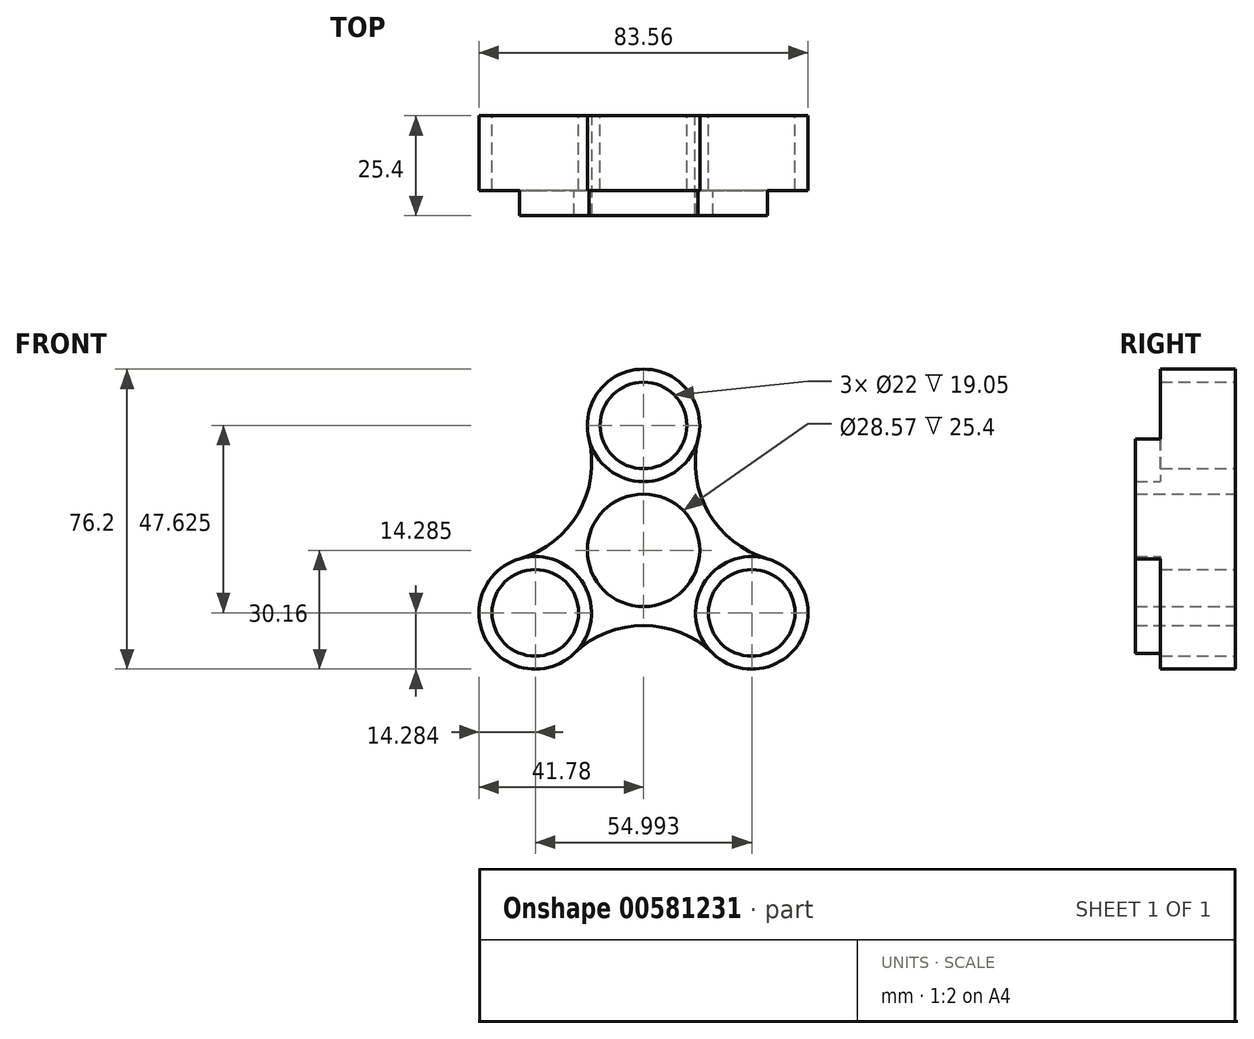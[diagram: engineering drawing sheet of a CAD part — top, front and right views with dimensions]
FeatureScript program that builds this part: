
annotation { "Feature Type Name" : "Feature", "Feature Type Description" : "" }
export const myFeature = defineFeature(function(context is Context, id is Id, definition is map)
    precondition{}
    {
        {
            var Q0;
            Q0=qCreatedBy(makeId("Front.planeOp"),FACE);
            var sketch = newSketch(context, id + "F0", { "sketchPlane" : qUnion([Q0])});
            skCircle(sketch, "E0", {"center": v(0, 0) * mm, "radius": 11 * mm});
            skCircle(sketch, "E1", {"center": v(0, 0) * mm, "radius": 14.29 * mm});
            skCircle(sketch, "E2", {"center": v(0, 31.75) * mm, "radius": 11 * mm});
            skCircle(sketch, "E3", {"center": v(0, 31.75) * mm, "radius": 14.29 * mm});
            skCircle(sketch, "E4.1.0", {"center": v(-27.5, -15.87) * mm, "radius": 11 * mm});
            skCircle(sketch, "E4.1.1", {"center": v(-27.5, -15.87) * mm, "radius": 14.29 * mm});
            skCircle(sketch, "E4.2.0", {"center": v(27.5, -15.88) * mm, "radius": 11 * mm});
            skCircle(sketch, "E4.2.1", {"center": v(27.5, -15.88) * mm, "radius": 14.29 * mm});
            skSolve(sketch);
        }
        {
            var Q0;
            Q0=qCreatedBy(makeId("Front.planeOp"),FACE);
            var sketch = newSketch(context, id + "F1", { "sketchPlane" : qUnion([Q0])});
            skCircle(sketch, "E5.0", {"center": v(0, 31.75) * mm, "radius": 14.29 * mm});
            skCircle(sketch, "E6.0", {"center": v(-27.5, -15.87) * mm, "radius": 14.29 * mm});
            skCircle(sketch, "E7.0", {"center": v(27.5, -15.88) * mm, "radius": 14.29 * mm});
            skCircle(sketch, "E8.0", {"center": v(0, 0) * mm, "radius": 14.29 * mm});
            skArc(sketch, "E9", {"start": v(-31.47, -2.15) * mm, "mid": v(-16.54, 9.55) * mm, "end": v(-13.87, 28.33) * mm});
            skArc(sketch, "E10", {"start": v(13.87, 28.33) * mm, "mid": v(16.54, 9.55) * mm, "end": v(31.47, -2.15) * mm});
            skArc(sketch, "E11", {"start": v(17.6, -26.18) * mm, "mid": v(0, -19.1) * mm, "end": v(-17.6, -26.18) * mm});
            skSolve(sketch);
        }
        {
            var Q0;
            Q0=makeQuery(id+"F1.imprint","IMPRINT",FACE,{"disambiguationData":[TD([[makeQuery(id+"F1.imprint","IMPRINT",EDGE,{"derivedFrom":sQuery(id+"F1.wireOp",EDGE,"E8.0")}),-1.0]])]});
            extrude(context, id + "F2", {"entities" : qUnion([Q0]), "depth" : 25.4 * mm, "offsetDistance" : 25.4 * mm});
        }
        {
            var Q0;
            Q0=makeQuery(id+"F0.imprint","IMPRINT",FACE,{"disambiguationData":[TD([[makeQuery(id+"F0.imprint","IMPRINT",EDGE,{"derivedFrom":sQuery(id+"F0.wireOp",EDGE,"E2")}),-1.0]])]});
            var Q1;
            Q1=makeQuery(id+"F0.imprint","IMPRINT",FACE,{"disambiguationData":[TD([[makeQuery(id+"F0.imprint","IMPRINT",EDGE,{"derivedFrom":sQuery(id+"F0.wireOp",EDGE,"E4.2.0")}),-1.0]])]});
            var Q2;
            Q2=makeQuery(id+"F0.imprint","IMPRINT",FACE,{"disambiguationData":[TD([[makeQuery(id+"F0.imprint","IMPRINT",EDGE,{"derivedFrom":sQuery(id+"F0.wireOp",EDGE,"E4.1.0")}),-1.0]])]});
            extrude(context, id + "F3", {"entities" : qUnion([Q0, Q1, Q2]), "operationType" : NewBodyOperationType.ADD, "depth" : 19.05 * mm, "offsetDistance" : 25.4 * mm});
        }
    });
